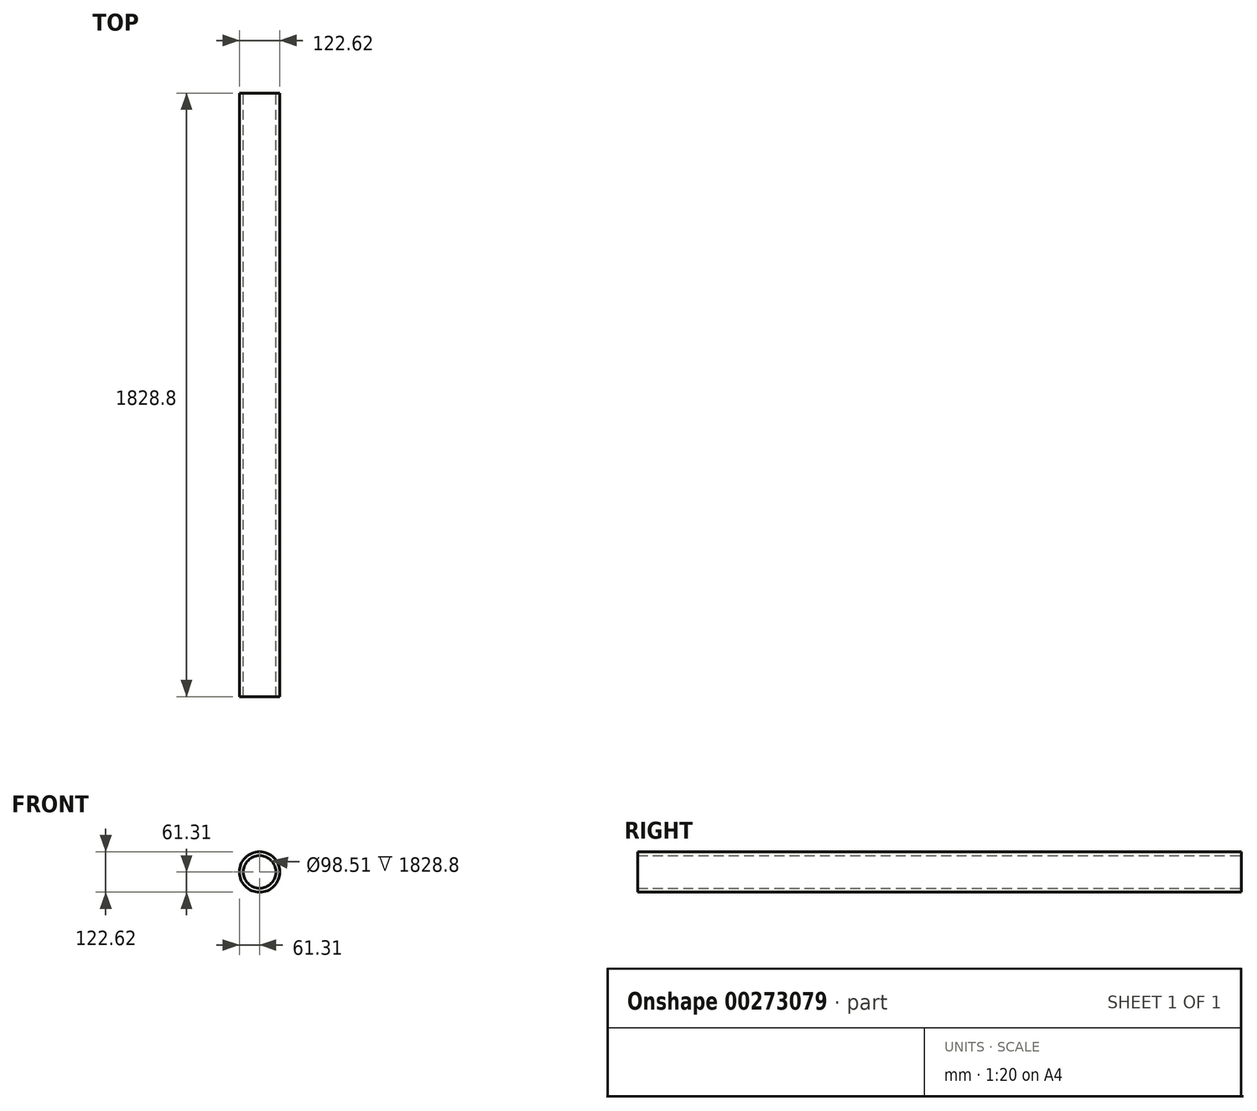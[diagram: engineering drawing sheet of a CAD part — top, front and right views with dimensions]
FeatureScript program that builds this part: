
annotation { "Feature Type Name" : "Feature", "Feature Type Description" : "" }
export const myFeature = defineFeature(function(context is Context, id is Id, definition is map)
    precondition{}
    {
        {
            var Q0;
            Q0=qCreatedBy(makeId("Front.planeOp"),FACE);
            var sketch = newSketch(context, id + "F0", { "sketchPlane" : qUnion([Q0])});
            skCircle(sketch, "E0", {"center": v(0, 0) * mm, "radius": 61.3 * mm});
            skCircle(sketch, "E1", {"center": v(0, 0) * mm, "radius": 49.25 * mm});
            skSolve(sketch);
        }
        {
            var Q0;
            Q0 = qSketchRegion(id + "F0", true);
            extrude(context, id + "F1", {"entities" : qUnion([Q0]), "depth" : 1828.8 * mm});
        }
    });
